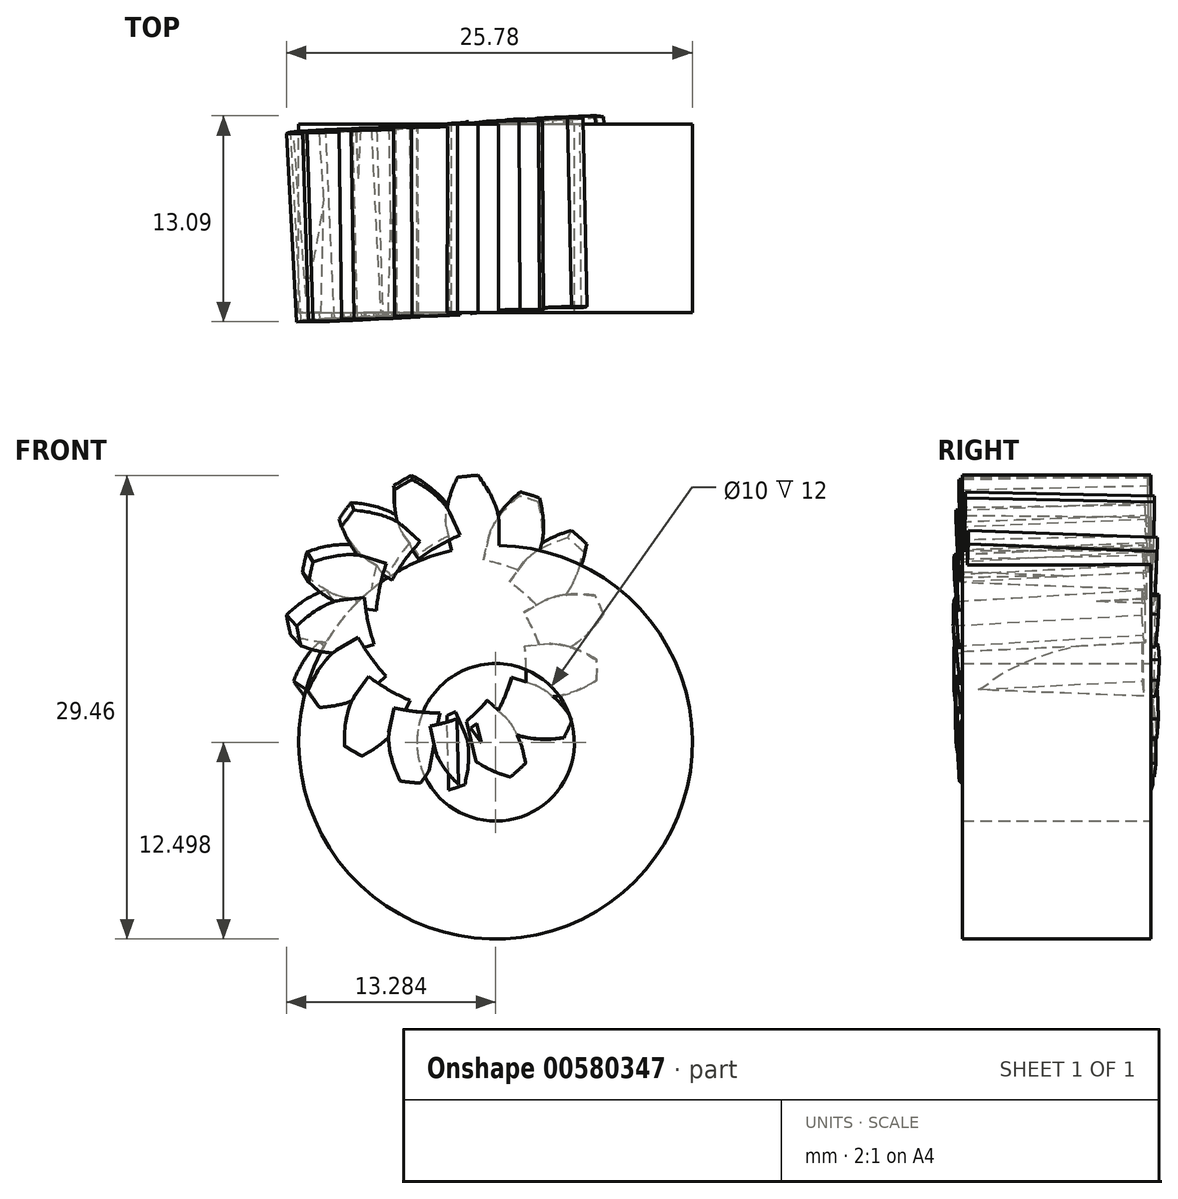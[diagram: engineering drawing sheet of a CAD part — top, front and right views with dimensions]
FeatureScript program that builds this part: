
annotation { "Feature Type Name" : "Feature", "Feature Type Description" : "" }
export const myFeature = defineFeature(function(context is Context, id is Id, definition is map)
    precondition{}
    {
        {
            assignVariable(context, id + "F0", {"name" : "module", "anyValue" : 2});
        }
        {
            assignVariable(context, id + "F1", {"name" : "pitchDiameter", "anyValue" : 30});
        }
        {
            assignVariable(context, id + "F2", {"name" : "numberOfTeeth", "anyValue" : getVariable(context, 'pitchDiameter') / getVariable(context, 'module')});
        }
        {
            assignVariable(context, id + "F3", {"name" : "thickness", "anyValue" : 12});
        }
        {
            var Q0;
            Q0=qCreatedBy(makeId("Front.planeOp"),FACE);
            var sketch = newSketch(context, id + "F4", { "sketchPlane" : qUnion([Q0])});
            skCircle(sketch, "E0", {"center": v(-37.02, 41.5) * mm, "radius": 15 * mm, "construction": true});
            skLineSegment(sketch, "E1", {"start": v(-37.02, 41.5) * mm, "end": v(-37.02, 66.5) * mm, "construction": true});
            skPoint(sketch, "E2", {"position": v(-37.02, 56.5) * mm});
            skLineSegment(sketch, "E3", {"start": v(-66.46, 56.5) * mm, "end": v(-7.57, 56.5) * mm, "construction": true});
            skLineSegment(sketch, "E4", {"start": v(-62.92, 47.08) * mm, "end": v(-11.11, 65.94) * mm, "construction": true});
            skLineSegment(sketch, "E5", {"start": v(-37.02, 41.5) * mm, "end": v(-41.84, 54.75) * mm, "construction": true});
            skCircle(sketch, "E6", {"center": v(-37.02, 41.5) * mm, "radius": 14.1 * mm, "construction": true});
            skArc(sketch, "E7", {"start": v(-41.84, 54.75) * mm, "mid": v(-43.83, 53.85) * mm, "end": v(-45.65, 52.65) * mm, "construction": true});
            skLineSegment(sketch, "E8", {"start": v(-45.65, 52.65) * mm, "end": v(-37.02, 41.5) * mm, "construction": true});
            skLineSegment(sketch, "E9", {"start": v(-45.65, 52.65) * mm, "end": v(-38.14, 58.47) * mm, "construction": true});
            skArc(sketch, "E10", {"start": v(-41.84, 54.75) * mm, "mid": v(-40.51, 55.16) * mm, "end": v(-39.16, 55.44) * mm, "construction": true});
            skLineSegment(sketch, "E11", {"start": v(-39.16, 55.44) * mm, "end": v(-37.02, 41.5) * mm, "construction": true});
            skLineSegment(sketch, "E12", {"start": v(-39.16, 55.44) * mm, "end": v(-36.83, 55.8) * mm, "construction": true});
            skArc(sketch, "E13", {"start": v(-36.8, 55.6) * mm, "mid": v(-39.36, 55.4) * mm, "end": v(-41.84, 54.75) * mm, "construction": true});
            skArc(sketch, "E14", {"start": v(-40.75, 55.1) * mm, "mid": v(-41.3, 54.94) * mm, "end": v(-41.84, 54.75) * mm, "construction": true});
            skLineSegment(sketch, "E15", {"start": v(-40.75, 55.1) * mm, "end": v(-37.02, 41.5) * mm, "construction": true});
            skLineSegment(sketch, "E16", {"start": v(-40.75, 55.1) * mm, "end": v(-36.9, 56.16) * mm, "construction": true});
            skArc(sketch, "E17", {"start": v(-41.84, 54.75) * mm, "mid": v(-41.58, 54.85) * mm, "end": v(-41.31, 54.93) * mm});
            skLineSegment(sketch, "E18", {"start": v(-41.31, 54.93) * mm, "end": v(-37.02, 41.5) * mm, "construction": true});
            skLineSegment(sketch, "E19", {"start": v(-41.31, 54.93) * mm, "end": v(-36.95, 56.33) * mm, "construction": true});
            skArc(sketch, "E20", {"start": v(-41.84, 54.75) * mm, "mid": v(-40.96, 55.04) * mm, "end": v(-40.07, 55.27) * mm});
            skLineSegment(sketch, "E21", {"start": v(-40.07, 55.27) * mm, "end": v(-37.02, 41.5) * mm, "construction": true});
            skLineSegment(sketch, "E22", {"start": v(-40.07, 55.27) * mm, "end": v(-36.86, 55.98) * mm, "construction": true});
            skArc(sketch, "E23", {"start": v(-41.84, 54.75) * mm, "mid": v(-43.34, 54.1) * mm, "end": v(-44.76, 53.28) * mm});
            skLineSegment(sketch, "E24", {"start": v(-44.76, 53.28) * mm, "end": v(-37.02, 41.5) * mm, "construction": true});
            skLineSegment(sketch, "E25", {"start": v(-44.76, 53.28) * mm, "end": v(-37.73, 57.9) * mm, "construction": true});
            skArc(sketch, "E26", {"start": v(-41.84, 54.75) * mm, "mid": v(-42.85, 54.34) * mm, "end": v(-43.83, 53.85) * mm});
            skLineSegment(sketch, "E27", {"start": v(-43.83, 53.85) * mm, "end": v(-37.02, 41.5) * mm, "construction": true});
            skLineSegment(sketch, "E28", {"start": v(-43.83, 53.85) * mm, "end": v(-37.42, 57.38) * mm, "construction": true});
            skArc(sketch, "E29", {"start": v(-41.84, 54.75) * mm, "mid": v(-42.35, 54.56) * mm, "end": v(-42.85, 54.34) * mm});
            skLineSegment(sketch, "E30", {"start": v(-42.85, 54.34) * mm, "end": v(-37.02, 41.5) * mm, "construction": true});
            skLineSegment(sketch, "E31", {"start": v(-42.85, 54.34) * mm, "end": v(-37.18, 56.92) * mm, "construction": true});
            skLineSegment(sketch, "E32", {"start": v(-38.14, 58.47) * mm, "end": v(-37.02, 41.5) * mm, "construction": true});
            skSolve(sketch);
        }
        {
            var Q0;
            Q0=qCreatedBy(makeId("Front.planeOp"),FACE);
            var sketch = newSketch(context, id + "F5", { "sketchPlane" : qUnion([Q0])});
            skPoint(sketch, "E33", {"position": v(-37.02, 56.5) * mm});
            skPoint(sketch, "E34", {"position": v(-37.02, 41.5) * mm});
            skLineSegment(sketch, "E35", {"start": v(-37.02, 41.5) * mm, "end": v(-39.32, 63.39) * mm, "construction": true});
            skCircle(sketch, "E36", {"center": v(-37.02, 41.5) * mm, "radius": 14.1 * mm, "construction": true});
            skPoint(sketch, "E37", {"position": v(-37.02, 63.5) * mm});
            skLineSegment(sketch, "E38", {"start": v(-37.02, 63.5) * mm, "end": v(-37.02, 41.5) * mm, "construction": true});
            skCircle(sketch, "E39", {"center": v(-37.02, 41.5) * mm, "radius": 12.5 * mm, "construction": true});
            skPoint(sketch, "E40.0", {"position": v(-37.42, 57.38) * mm});
            skPoint(sketch, "E41.0", {"position": v(-37.18, 56.92) * mm});
            skPoint(sketch, "E42.0", {"position": v(-37.73, 57.9) * mm});
            skPoint(sketch, "E43.0", {"position": v(-36.95, 56.33) * mm});
            skPoint(sketch, "E44.0", {"position": v(-36.9, 56.16) * mm});
            skPoint(sketch, "E45.0", {"position": v(-36.86, 55.98) * mm});
            skPoint(sketch, "E46.0", {"position": v(-36.83, 55.8) * mm});
            skPoint(sketch, "E47.0", {"position": v(-36.8, 55.6) * mm});
            skPoint(sketch, "E48.0", {"position": v(-38.14, 58.47) * mm});
            skFitSpline(sketch, "E49", {"points": [v(-36.8, 55.6) * mm, v(-36.83, 55.8) * mm, v(-36.86, 55.98) * mm, v(-36.9, 56.16) * mm, v(-36.95, 56.33) * mm, v(-37.02, 56.5) * mm, v(-37.18, 56.92) * mm, v(-37.42, 57.38) * mm, v(-37.73, 57.9) * mm, v(-38.14, 58.47) * mm], "startDerivative": vector(-1.9, 7.64) * mm, "endDerivative": vector(-3.3, 4.96) * mm});
            skArc(sketch, "E50", {"start": v(-38.14, 58.47) * mm, "mid": v(-38.47, 58.45) * mm, "end": v(-38.8, 58.41) * mm});
            skFitSpline(sketch, "E51.MirrorCS", {"points": [v(-40.15, 55.25) * mm, v(-40.17, 55.45) * mm, v(-40.18, 55.63) * mm, v(-40.17, 55.81) * mm, v(-40.16, 56) * mm, v(-40.13, 56.18) * mm, v(-40.06, 56.61) * mm, v(-39.92, 57.12) * mm, v(-39.72, 57.7) * mm, v(-39.44, 58.33) * mm], "startDerivative": vector(0.28, 7.87) * mm, "endDerivative": vector(2.2, 5.54) * mm});
            skArc(sketch, "E52.MirrorCS", {"start": v(-39.44, 58.33) * mm, "mid": v(-39.12, 58.38) * mm, "end": v(-38.8, 58.41) * mm});
            skLineSegment(sketch, "E53", {"start": v(-36.8, 55.6) * mm, "end": v(-36.8, 54) * mm});
            skArc(sketch, "E54", {"start": v(-36.8, 54) * mm, "mid": v(-37.57, 54) * mm, "end": v(-38.32, 53.94) * mm});
            skLineSegment(sketch, "E55.MirrorCS", {"start": v(-40.15, 55.25) * mm, "end": v(-39.82, 53.69) * mm});
            skArc(sketch, "E56.MirrorCS", {"start": v(-39.82, 53.69) * mm, "mid": v(-39.08, 53.84) * mm, "end": v(-38.32, 53.94) * mm});
            skSolve(sketch);
        }
        {
            var Q0;
            Q0=qCreatedBy(makeId("Front.planeOp"),FACE);
            var sketch = newSketch(context, id + "F6", { "sketchPlane" : qUnion([Q0])});
            skCircle(sketch, "E57.0", {"center": v(-37.02, 41.5) * mm, "radius": 12.5 * mm});
            skFitSpline(sketch, "E58.1.0", {"points": [v(-39.44, 58.37) * mm, v(-39.55, 58.09) * mm, v(-39.7, 57.8) * mm, v(-39.9, 57.19) * mm, v(-40.05, 56.7) * mm, v(-40.15, 56.26) * mm, v(-40.18, 56.02) * mm, v(-40.21, 55.78) * mm, v(-40.23, 55.57) * mm, v(-40.25, 55.25) * mm, v(-40.2, 55.32) * mm, v(-40.22, 55.07) * mm]});
            skLineSegment(sketch, "E58.1.1", {"start": v(-40.15, 55.25) * mm, "end": v(-39.82, 53.69) * mm});
            skArc(sketch, "E58.1.2", {"start": v(-39.82, 53.69) * mm, "mid": v(-39.08, 53.84) * mm, "end": v(-38.32, 53.94) * mm});
            skArc(sketch, "E58.1.3", {"start": v(-38.32, 53.94) * mm, "mid": v(-37.57, 54) * mm, "end": v(-36.8, 54) * mm});
            skLineSegment(sketch, "E58.1.4", {"start": v(-36.8, 54) * mm, "end": v(-36.8, 55.6) * mm});
            skFitSpline(sketch, "E58.1.5", {"points": [v(-36.75, 55.36) * mm, v(-36.8, 55.6) * mm, v(-36.75, 55.54) * mm, v(-36.82, 55.86) * mm, v(-36.87, 56.06) * mm, v(-36.94, 56.29) * mm, v(-37.02, 56.51) * mm, v(-37.19, 56.94) * mm, v(-37.4, 57.4) * mm, v(-37.7, 57.96) * mm, v(-37.9, 58.22) * mm, v(-38.06, 58.48) * mm]});
            skArc(sketch, "E58.1.6", {"start": v(-38.14, 58.47) * mm, "mid": v(-38.47, 58.45) * mm, "end": v(-38.8, 58.41) * mm});
            skArc(sketch, "E58.1.7", {"start": v(-38.8, 58.41) * mm, "mid": v(-39.12, 58.38) * mm, "end": v(-39.44, 58.33) * mm});
            skSolve(sketch);
        }
        {
            var Q0;
            {var subQ0=sQuery(id+"F6.wireOp",EDGE,"E57.0");var subQ1=makeQuery(id+"F6.imprint","INTERSECT",VERTEX,{"derivedFrom":[subQ0,sQuery(id+"F6.wireOp",EDGE,"E58.1.1")]});Q0=makeQuery(id+"F6.imprint","IMPRINT",FACE,{"disambiguationData":[TD([[makeQuery(id+"F6.imprint","IMPRINT",EDGE,{"disambiguationData":[TD([[subQ1,1.0]])],"derivedFrom":subQ0}),1.0]])]});}
            extrude(context, id + "F7", {"entities" : qUnion([Q0]), "depth" : (getVariable(context, 'thickness')) * mm, "offsetDistance" : 25 * mm});
        }
        {
            var Q0;
            Q0=makeQuery(id+"F5.imprint","IMPRINT",FACE,{"disambiguationData":[TD([[makeQuery(id+"F5.imprint","IMPRINT",EDGE,{"derivedFrom":sQuery(id+"F5.wireOp",EDGE,"E49")}),1.0]])]});
            extrude(context, id + "F8", {"entities" : qUnion([Q0]), "depth" : (getVariable(context, 'thickness')) * mm, "offsetDistance" : 25 * mm});
        }
        {
            var Q0;
            Q0=makeQuery(id+"F8.opExtrude","CAP_EDGE",EDGE,{"disambiguationData":[OSD([sQuery(id+"F5.wireOp",EDGE,"E50"),sQuery(id+"F5.wireOp",EDGE,"E52.MirrorCS")])],"isStart":false});
            cPoint(context, id + "F9", {"entities" : qUnion([Q0]), "parameter" : 0.5});
        }
        {
            var Q0;
            Q0=qCreatedBy(id+"F9",VERTEX);
            var Q1;
            Q1=sQuery(id+"F5.wireOp",VERTEX,"E52.MirrorCS.end");
            var Q2;
            Q2=sQuery(id+"F5.wireOp",VERTEX,"E56.MirrorCS.end");
            cPlane(context, id + "F10", {"entities" : qUnion([Q0, Q1, Q2]), "cplaneType" : CPlaneType.THREE_POINT, "offset" : 0 * mm, "width" : 150 * mm, "height" : 150 * mm});
        }
        {
            var Q0;
            Q0=qCreatedBy(id+"F10.planeOp",FACE);
            var sketch = newSketch(context, id + "F11", { "sketchPlane" : qUnion([Q0])});
            skPoint(sketch, "E59.0", {"position": v(0, 45.15) * mm});
            skLineSegment(sketch, "E60", {"start": v(0, 45.15) * mm, "end": v(30.78, 45.15) * mm, "construction": true});
            skSolve(sketch);
        }
        {
            var Q0;
            Q0=makeQuery(id+"F8.opExtrude","SWEPT_BODY",BODY,{"disambiguationData":[OSD([sQuery(id+"F5.wireOp",EDGE,"E49"),sQuery(id+"F5.wireOp",EDGE,"E50"),sQuery(id+"F5.wireOp",EDGE,"E51.MirrorCS"),sQuery(id+"F5.wireOp",EDGE,"E52.MirrorCS"),sQuery(id+"F5.wireOp",EDGE,"E53"),sQuery(id+"F5.wireOp",EDGE,"E54"),sQuery(id+"F5.wireOp",EDGE,"E55.MirrorCS"),sQuery(id+"F5.wireOp",EDGE,"E56.MirrorCS")])]});
            var Q1;
            Q1=sQuery(id+"F11.wireOp",EDGE,"E60");
            circularPattern(context, id + "F12", {"operationType" : NewBodyOperationType.ADD, "entities" : qUnion([Q0]), "axis" : qUnion([Q1]), "angle" : 360 * degree, "instanceCount" : getVariable(context, 'numberOfTeeth'), "equalSpace" : true});
        }
        {
            var Q0;
            Q0=qCreatedBy(makeId("Front.planeOp"),FACE);
            var sketch = newSketch(context, id + "F13", { "sketchPlane" : qUnion([Q0])});
            skPoint(sketch, "E61.0", {"position": v(-37.02, 41.5) * mm});
            skCircle(sketch, "E62", {"center": v(-37.02, 41.5) * mm, "radius": 5 * mm});
            skSolve(sketch);
        }
        {
            var Q0;
            Q0=makeQuery(id+"F13.imprint","IMPRINT",FACE,{"disambiguationData":[TD([[makeQuery(id+"F13.imprint","IMPRINT",EDGE,{"derivedFrom":sQuery(id+"F13.wireOp",EDGE,"E62")}),1.0]])]});
            extrude(context, id + "F14", {"entities" : qUnion([Q0]), "operationType" : NewBodyOperationType.REMOVE, "depth" : (getVariable(context, 'thickness')) * mm, "offsetDistance" : 25 * mm});
        }
    });
